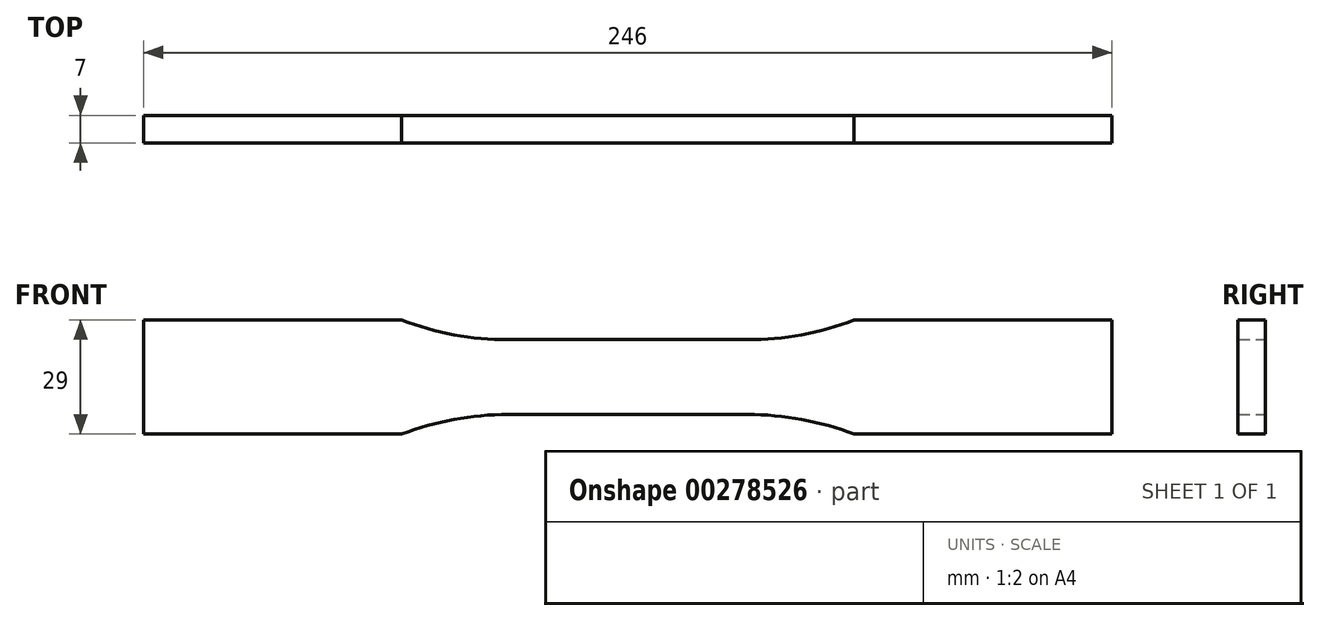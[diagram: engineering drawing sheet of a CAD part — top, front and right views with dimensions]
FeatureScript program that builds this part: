
annotation { "Feature Type Name" : "Feature", "Feature Type Description" : "" }
export const myFeature = defineFeature(function(context is Context, id is Id, definition is map)
    precondition{}
    {
        {
            var Q0;
            Q0=qCreatedBy(makeId("Front.planeOp"),FACE);
            var sketch = newSketch(context, id + "F0", { "sketchPlane" : qUnion([Q0])});
            skLineSegment(sketch, "E0", {"start": v(0, 9.5) * mm, "end": v(30.39, 9.5) * mm});
            skArc(sketch, "E1", {"start": v(30.39, 9.5) * mm, "mid": v(44.17, 10.76) * mm, "end": v(57.5, 14.5) * mm});
            skLineSegment(sketch, "E2", {"start": v(57.5, 14.5) * mm, "end": v(123, 14.5) * mm});
            skLineSegment(sketch, "E3.MirrorCS", {"start": v(57.5, -14.5) * mm, "end": v(123, -14.5) * mm});
            skLineSegment(sketch, "E4.MirrorCS", {"start": v(0, -9.5) * mm, "end": v(30.39, -9.5) * mm});
            skArc(sketch, "E5.MirrorCS", {"start": v(30.39, -9.5) * mm, "mid": v(44.17, -10.76) * mm, "end": v(57.5, -14.5) * mm});
            skLineSegment(sketch, "E6.MirrorCS", {"start": v(0, -9.5) * mm, "end": v(-30.39, -9.5) * mm});
            skArc(sketch, "E7.MirrorCS", {"start": v(-30.39, 9.5) * mm, "mid": v(-44.17, 10.76) * mm, "end": v(-57.5, 14.5) * mm});
            skLineSegment(sketch, "E8.MirrorCS", {"start": v(-57.5, 14.5) * mm, "end": v(-123, 14.5) * mm});
            skLineSegment(sketch, "E9.MirrorCS", {"start": v(-57.5, -14.5) * mm, "end": v(-123, -14.5) * mm});
            skLineSegment(sketch, "E10.MirrorCS", {"start": v(0, 9.5) * mm, "end": v(-30.39, 9.5) * mm});
            skArc(sketch, "E11.MirrorCS", {"start": v(-30.39, -9.5) * mm, "mid": v(-44.17, -10.76) * mm, "end": v(-57.5, -14.5) * mm});
            skLineSegment(sketch, "E12", {"start": v(-123, 14.5) * mm, "end": v(-123, -14.5) * mm});
            skLineSegment(sketch, "E13", {"start": v(123, 14.5) * mm, "end": v(123, -14.5) * mm});
            skSolve(sketch);
        }
        {
            var Q0;
            Q0=makeQuery(id+"F0.imprint","IMPRINT",FACE,{"disambiguationData":[TD([[makeQuery(id+"F0.imprint","IMPRINT",EDGE,{"derivedFrom":sQuery(id+"F0.wireOp",EDGE,"E4.MirrorCS")}),1.0]])]});
            extrude(context, id + "F1", {"entities" : qUnion([Q0]), "endBound" : BoundingType.SYMMETRIC, "depth" : 7 * mm});
        }
    });
